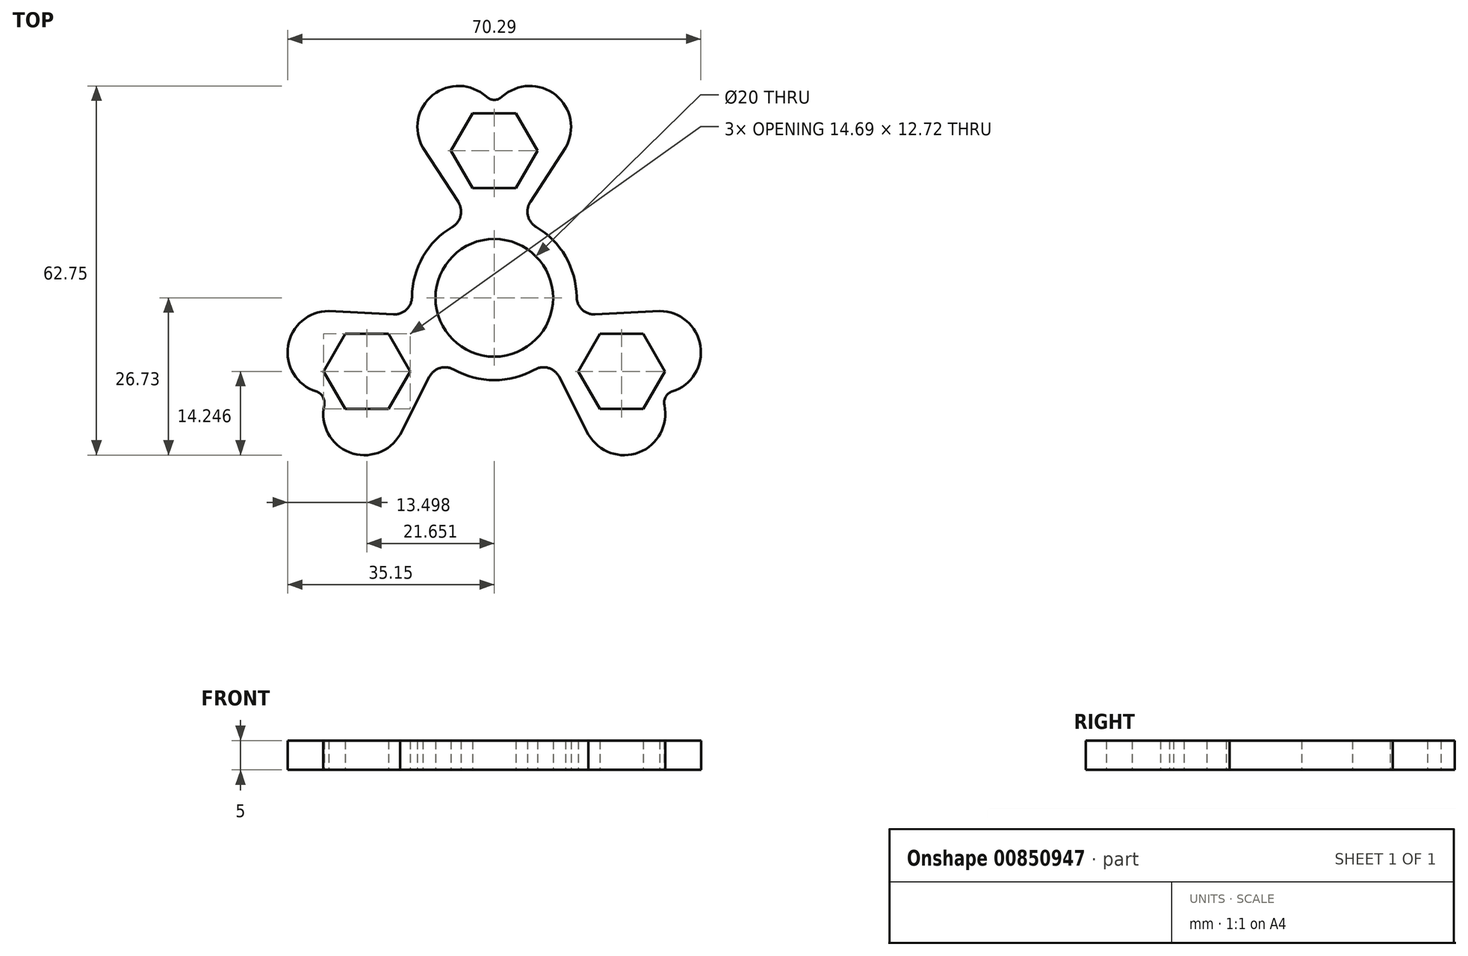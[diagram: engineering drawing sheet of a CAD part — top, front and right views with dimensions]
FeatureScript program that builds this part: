
annotation { "Feature Type Name" : "Feature", "Feature Type Description" : "" }
export const myFeature = defineFeature(function(context is Context, id is Id, definition is map)
    precondition{}
    {
        {
            var Q0;
            Q0=qCreatedBy(makeId("Top.planeOp"),FACE);
            var sketch = newSketch(context, id + "F0", { "sketchPlane" : qUnion([Q0])});
            skLineSegment(sketch, "E0", {"start": v(6.13, 16.29) * mm, "end": v(12.12, 25.52) * mm});
            skArc(sketch, "E1", {"start": v(12.12, 25.52) * mm, "mid": v(10.45, 34.47) * mm, "end": v(1.35, 34.19) * mm});
            skLineSegment(sketch, "E2.trimOffspring", {"start": v(0, 32.52) * mm, "end": v(0, 67.12) * mm, "construction": true});
            skLineSegment(sketch, "E3.trimOffspring", {"start": v(0, 19.02) * mm, "end": v(0, 41.02) * mm, "construction": true});
            skArc(sketch, "E4.MirrorCS", {"start": v(-12.13, 25.52) * mm, "mid": v(-10.45, 34.47) * mm, "end": v(-1.35, 34.19) * mm});
            skPoint(sketch, "E5.visualSharp", {"position": v(0, 32.52) * mm});
            skArc(sketch, "E5.filletArc", {"start": v(-1.35, 34.19) * mm, "mid": v(0, 33.67) * mm, "end": v(1.35, 34.19) * mm});
            skCircle(sketch, "E6.cCircle", {"center": v(0, 25.02) * mm, "radius": 6.36 * mm, "construction": true});
            skLineSegment(sketch, "E6.0", {"start": v(-3.67, 31.38) * mm, "end": v(3.67, 31.38) * mm});
            skLineSegment(sketch, "E6.1", {"start": v(3.67, 31.38) * mm, "end": v(7.34, 25.02) * mm});
            skLineSegment(sketch, "E6.2", {"start": v(7.34, 25.02) * mm, "end": v(3.67, 18.66) * mm});
            skLineSegment(sketch, "E6.3", {"start": v(3.67, 18.66) * mm, "end": v(-3.67, 18.66) * mm});
            skLineSegment(sketch, "E6.4", {"start": v(-3.67, 18.66) * mm, "end": v(-7.35, 25.02) * mm});
            skLineSegment(sketch, "E6.5", {"start": v(-7.35, 25.02) * mm, "end": v(-3.67, 31.38) * mm});
            skPoint(sketch, "E6.0.midPoint", {"position": v(0, 31.38) * mm});
            skCircle(sketch, "E7.0", {"center": v(0, 0.02) * mm, "radius": 14 * mm});
            skArc(sketch, "E8", {"start": v(6.13, 16.29) * mm, "mid": v(5.72, 13.97) * mm, "end": v(7.12, 12.07) * mm});
            skPoint(sketch, "E9.orphan", {"position": v(1.19, 8.67) * mm});
            skPoint(sketch, "E10.orphan", {"position": v(-1.19, 8.67) * mm});
            skArc(sketch, "E11.MirrorCS", {"start": v(-6.13, 16.29) * mm, "mid": v(-5.73, 13.97) * mm, "end": v(-7.12, 12.07) * mm});
            skLineSegment(sketch, "E12", {"start": v(-6.13, 16.29) * mm, "end": v(-12.13, 25.52) * mm});
            skLineSegment(sketch, "E13.1.0", {"start": v(-25.32, -6.12) * mm, "end": v(-17.98, -6.12) * mm});
            skPoint(sketch, "E13.1.1", {"position": v(-28.15, -16.23) * mm});
            skPoint(sketch, "E13.1.2", {"position": v(-27.16, -15.66) * mm});
            skPoint(sketch, "E13.1.3", {"position": v(-8.1, -3.29) * mm});
            skArc(sketch, "E13.1.4", {"start": v(-28.15, -2.23) * mm, "mid": v(-35.06, -8.16) * mm, "end": v(-30.27, -15.9) * mm});
            skCircle(sketch, "E13.1.5", {"center": v(-21.65, -12.48) * mm, "radius": 6.36 * mm, "construction": true});
            skArc(sketch, "E13.1.6", {"start": v(-17.16, -2.81) * mm, "mid": v(-14.95, -2) * mm, "end": v(-14, 0.16) * mm});
            skLineSegment(sketch, "E13.1.7", {"start": v(-11.03, -13.43) * mm, "end": v(-16.02, -23.23) * mm});
            skLineSegment(sketch, "E13.1.8", {"start": v(-16.46, -9.48) * mm, "end": v(-35.5, -20.48) * mm, "construction": true});
            skLineSegment(sketch, "E13.1.9", {"start": v(-14.3, -12.48) * mm, "end": v(-17.98, -18.84) * mm});
            skLineSegment(sketch, "E13.1.10", {"start": v(-29, -12.48) * mm, "end": v(-25.32, -6.12) * mm});
            skArc(sketch, "E13.1.11", {"start": v(-16.02, -23.23) * mm, "mid": v(-24.61, -26.26) * mm, "end": v(-28.92, -18.24) * mm});
            skLineSegment(sketch, "E13.1.12", {"start": v(-17.16, -2.81) * mm, "end": v(-28.15, -2.23) * mm});
            skLineSegment(sketch, "E13.1.13", {"start": v(-17.98, -18.84) * mm, "end": v(-25.32, -18.84) * mm});
            skPoint(sketch, "E13.1.14", {"position": v(-6.9, -5.34) * mm});
            skLineSegment(sketch, "E13.1.15", {"start": v(-17.98, -6.12) * mm, "end": v(-14.3, -12.48) * mm});
            skArc(sketch, "E13.1.16", {"start": v(-11.03, -13.43) * mm, "mid": v(-9.22, -11.92) * mm, "end": v(-6.88, -12.18) * mm});
            skArc(sketch, "E13.1.17", {"start": v(-28.92, -18.24) * mm, "mid": v(-29.14, -16.81) * mm, "end": v(-30.27, -15.9) * mm});
            skLineSegment(sketch, "E13.1.18", {"start": v(-25.32, -18.84) * mm, "end": v(-29, -12.48) * mm});
            skLineSegment(sketch, "E13.2.0", {"start": v(17.98, -18.84) * mm, "end": v(14.3, -12.48) * mm});
            skPoint(sketch, "E13.2.1", {"position": v(28.14, -16.23) * mm});
            skPoint(sketch, "E13.2.2", {"position": v(27.16, -15.66) * mm});
            skPoint(sketch, "E13.2.3", {"position": v(6.9, -5.34) * mm});
            skArc(sketch, "E13.2.4", {"start": v(16.02, -23.23) * mm, "mid": v(24.61, -26.26) * mm, "end": v(28.92, -18.24) * mm});
            skCircle(sketch, "E13.2.5", {"center": v(21.65, -12.48) * mm, "radius": 6.36 * mm, "construction": true});
            skArc(sketch, "E13.2.6", {"start": v(11.02, -13.43) * mm, "mid": v(9.22, -11.92) * mm, "end": v(6.88, -12.18) * mm});
            skLineSegment(sketch, "E13.2.7", {"start": v(17.15, -2.81) * mm, "end": v(28.14, -2.23) * mm});
            skLineSegment(sketch, "E13.2.8", {"start": v(16.45, -9.48) * mm, "end": v(35.5, -20.48) * mm, "construction": true});
            skLineSegment(sketch, "E13.2.9", {"start": v(17.98, -6.12) * mm, "end": v(25.32, -6.12) * mm});
            skLineSegment(sketch, "E13.2.10", {"start": v(25.32, -18.84) * mm, "end": v(17.98, -18.84) * mm});
            skArc(sketch, "E13.2.11", {"start": v(28.14, -2.23) * mm, "mid": v(35.06, -8.16) * mm, "end": v(30.27, -15.9) * mm});
            skLineSegment(sketch, "E13.2.12", {"start": v(11.02, -13.43) * mm, "end": v(16.02, -23.23) * mm});
            skLineSegment(sketch, "E13.2.13", {"start": v(25.32, -6.12) * mm, "end": v(29, -12.48) * mm});
            skPoint(sketch, "E13.2.14", {"position": v(8.1, -3.29) * mm});
            skLineSegment(sketch, "E13.2.15", {"start": v(14.3, -12.48) * mm, "end": v(17.98, -6.12) * mm});
            skArc(sketch, "E13.2.16", {"start": v(17.15, -2.81) * mm, "mid": v(14.94, -2) * mm, "end": v(14, 0.16) * mm});
            skArc(sketch, "E13.2.17", {"start": v(30.27, -15.9) * mm, "mid": v(29.14, -16.81) * mm, "end": v(28.92, -18.24) * mm});
            skLineSegment(sketch, "E13.2.18", {"start": v(29, -12.48) * mm, "end": v(25.32, -18.84) * mm});
            skCircle(sketch, "E14", {"center": v(0, 0) * mm, "radius": 10 * mm});
            skSolve(sketch);
        }
        {
            var Q0;
            Q0=makeQuery(id+"F0.imprint","IMPRINT",FACE,{"disambiguationData":[TD([[makeQuery(id+"F0.imprint","IMPRINT",EDGE,{"derivedFrom":sQuery(id+"F0.wireOp",EDGE,"E13.1.0")}),1.0]])]});
            var Q1;
            {var subQ0=sQuery(id+"F0.wireOp",EDGE,"E7.0");var subQ4=makeQuery(id+"F0.imprint","INTERSECT",VERTEX,{"derivedFrom":[subQ0,sQuery(id+"F0.wireOp",EDGE,"E8")]});Q1=makeQuery(id+"F0.imprint","IMPRINT",FACE,{"disambiguationData":[TD([[makeQuery(id+"F0.imprint","IMPRINT",EDGE,{"disambiguationData":[TD([[subQ4,1.0]])],"derivedFrom":subQ0}),1.0]])]});}
            var Q2;
            Q2=makeQuery(id+"F0.imprint","IMPRINT",FACE,{"disambiguationData":[TD([[makeQuery(id+"F0.imprint","IMPRINT",EDGE,{"derivedFrom":sQuery(id+"F0.wireOp",EDGE,"E13.2.0")}),1.0]])]});
            var Q3;
            Q3=makeQuery(id+"F0.imprint","IMPRINT",FACE,{"disambiguationData":[TD([[makeQuery(id+"F0.imprint","IMPRINT",EDGE,{"derivedFrom":sQuery(id+"F0.wireOp",EDGE,"E0")}),1.0]])]});
            extrude(context, id + "F1", {"entities" : qUnion([Q0, Q1, Q2, Q3]), "depth" : 5 * mm, "offsetDistance" : 25 * mm});
        }
    });
